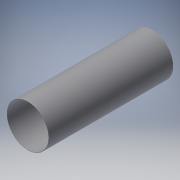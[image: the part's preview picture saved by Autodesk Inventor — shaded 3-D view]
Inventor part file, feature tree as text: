
AUTODESK INVENTOR PART (.ipt)
format: ipt  version: 2019 (Build 230136000, 136)  size: 100,352 bytes
history: native  units: mm
features: extrude x2, sketch x2
ambient origin geometry x8: Origin, YZ Plane, XZ Plane, XY Plane, X Axis, Y Axis, Z Axis, Center Point
bodies: Solid1 (feature_tree)
feature tree (4):
  extrude  "Extrusion1"  Depth=120.0mm TaperAngle=0.0deg
  extrude  "Extrusion2"  Depth=120.0mm TaperAngle=0.0deg
  sketch  "Sketch1"  dims[d0=40.536mm d1=120.0mm d2=0.0mm]
  sketch  "Sketch2"  dims[d3=40.0mm d4=120.0mm d5=0.0mm]
